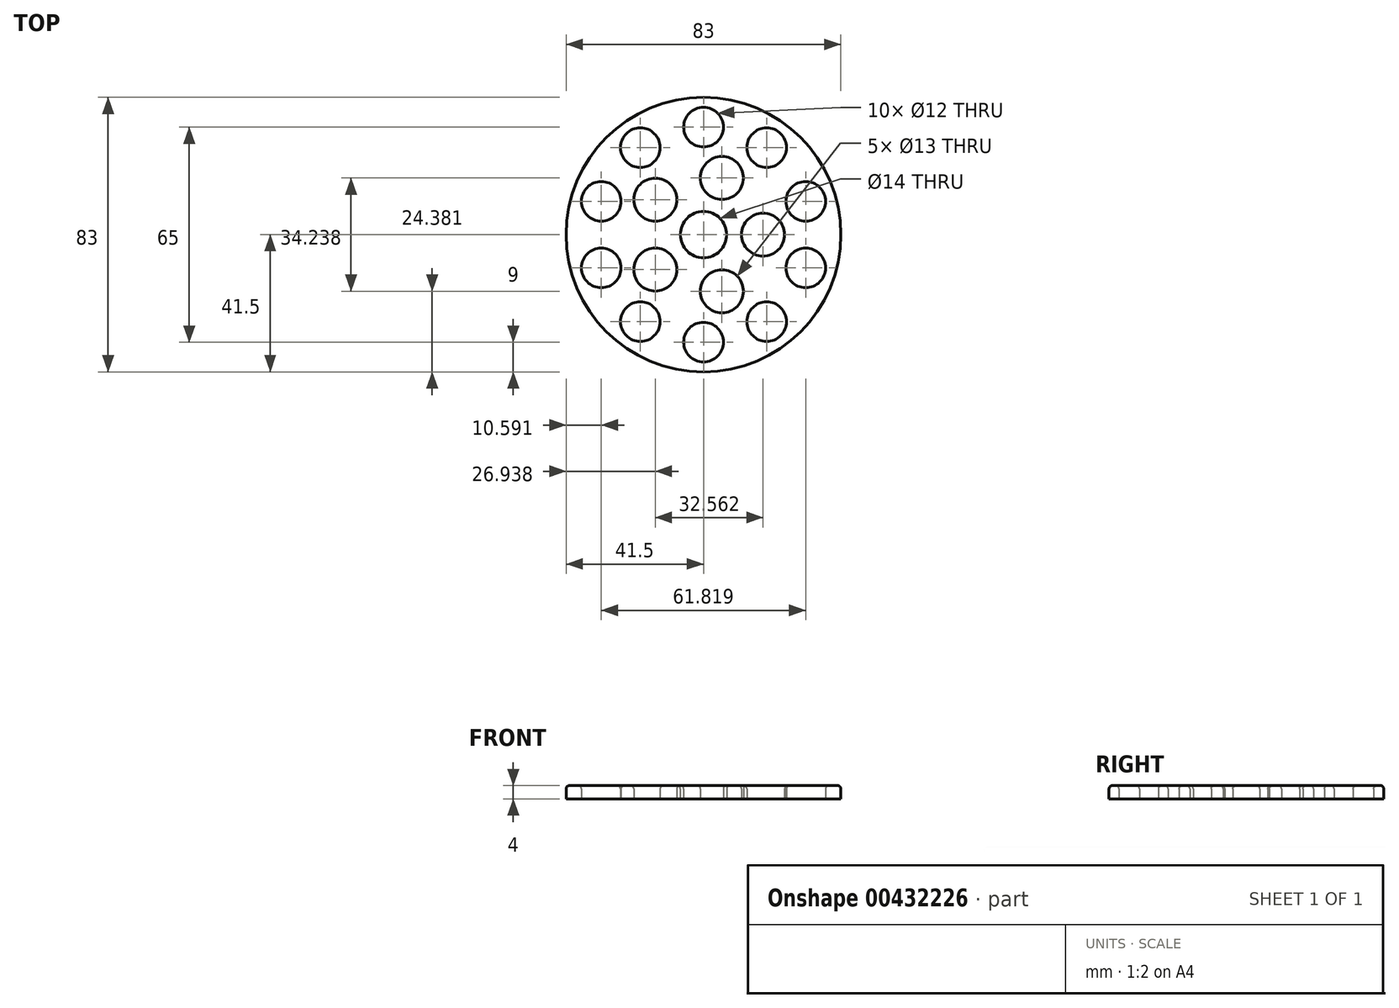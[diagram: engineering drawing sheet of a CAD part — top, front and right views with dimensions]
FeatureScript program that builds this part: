
annotation { "Feature Type Name" : "Feature", "Feature Type Description" : "" }
export const myFeature = defineFeature(function(context is Context, id is Id, definition is map)
    precondition{}
    {
        {
            var Q0;
            Q0=qCreatedBy(makeId("Top.planeOp"),FACE);
            var sketch = newSketch(context, id + "F0", { "sketchPlane" : qUnion([Q0])});
            skCircle(sketch, "E0", {"center": v(0, 0) * mm, "radius": 41.5 * mm});
            skCircle(sketch, "E1", {"center": v(0, 32.5) * mm, "radius": 6 * mm});
            skCircle(sketch, "E2.1.0", {"center": v(-19.1, 26.3) * mm, "radius": 6 * mm});
            skCircle(sketch, "E2.2.0", {"center": v(-30.9, 10.04) * mm, "radius": 6 * mm});
            skCircle(sketch, "E2.3.0", {"center": v(-30.9, -10.04) * mm, "radius": 6 * mm});
            skCircle(sketch, "E2.4.0", {"center": v(-19.1, -26.3) * mm, "radius": 6 * mm});
            skCircle(sketch, "E2.5.0", {"center": v(0, -32.5) * mm, "radius": 6 * mm});
            skCircle(sketch, "E2.6.0", {"center": v(19.1, -26.3) * mm, "radius": 6 * mm});
            skCircle(sketch, "E2.7.0", {"center": v(30.9, -10.04) * mm, "radius": 6 * mm});
            skCircle(sketch, "E2.8.0", {"center": v(30.9, 10.04) * mm, "radius": 6 * mm});
            skCircle(sketch, "E2.9.0", {"center": v(19.1, 26.3) * mm, "radius": 6 * mm});
            skCircle(sketch, "E3", {"center": v(0, 0) * mm, "radius": 7 * mm});
            skCircle(sketch, "E4", {"center": v(0, 0) * mm, "radius": 32.5 * mm, "construction": true});
            skCircle(sketch, "E5", {"center": v(0, 0) * mm, "radius": 18 * mm, "construction": true});
            skLineSegment(sketch, "E6", {"start": v(0, 0) * mm, "end": v(12.82, 39.47) * mm, "construction": true});
            skLineSegment(sketch, "E7", {"start": v(0, 0) * mm, "end": v(19.1, 26.3) * mm, "construction": true});
            skCircle(sketch, "E8", {"center": v(5.56, 17.12) * mm, "radius": 6.5 * mm});
            skCircle(sketch, "E9.1.0", {"center": v(-14.56, 10.58) * mm, "radius": 6.5 * mm});
            skCircle(sketch, "E9.2.0", {"center": v(-14.56, -10.58) * mm, "radius": 6.5 * mm});
            skCircle(sketch, "E9.3.0", {"center": v(5.56, -17.12) * mm, "radius": 6.5 * mm});
            skCircle(sketch, "E9.4.0", {"center": v(18, 0) * mm, "radius": 6.5 * mm});
            skSolve(sketch);
        }
        {
            var Q0;
            Q0 = qSketchRegion(id + "F0", true);
            extrude(context, id + "F1", {"entities" : qUnion([Q0]), "depth" : 4 * mm});
        }
        {
            var Q0;
            Q0=makeQuery(id+"F1.opExtrude","CAP_FACE",FACE,{"disambiguationData":[OSD([sQuery(id+"F0.wireOp",EDGE,"E0"),sQuery(id+"F0.wireOp",EDGE,"E1"),sQuery(id+"F0.wireOp",EDGE,"E2.1.0"),sQuery(id+"F0.wireOp",EDGE,"E2.2.0"),sQuery(id+"F0.wireOp",EDGE,"E2.3.0"),sQuery(id+"F0.wireOp",EDGE,"E2.4.0"),sQuery(id+"F0.wireOp",EDGE,"E2.5.0"),sQuery(id+"F0.wireOp",EDGE,"E2.6.0"),sQuery(id+"F0.wireOp",EDGE,"E2.7.0"),sQuery(id+"F0.wireOp",EDGE,"E2.8.0"),sQuery(id+"F0.wireOp",EDGE,"E2.9.0"),sQuery(id+"F0.wireOp",EDGE,"E3"),sQuery(id+"F0.wireOp",EDGE,"E8"),sQuery(id+"F0.wireOp",EDGE,"E9.1.0"),sQuery(id+"F0.wireOp",EDGE,"E9.2.0"),sQuery(id+"F0.wireOp",EDGE,"E9.3.0"),sQuery(id+"F0.wireOp",EDGE,"E9.4.0")])],"isStart":false});
            fillet(context, id + "F2", {"entities" : qUnion([Q0]), "radius" : 1 * mm, "tangentPropagation" : true, "allowEdgeOverflow" : false});
        }
    });
